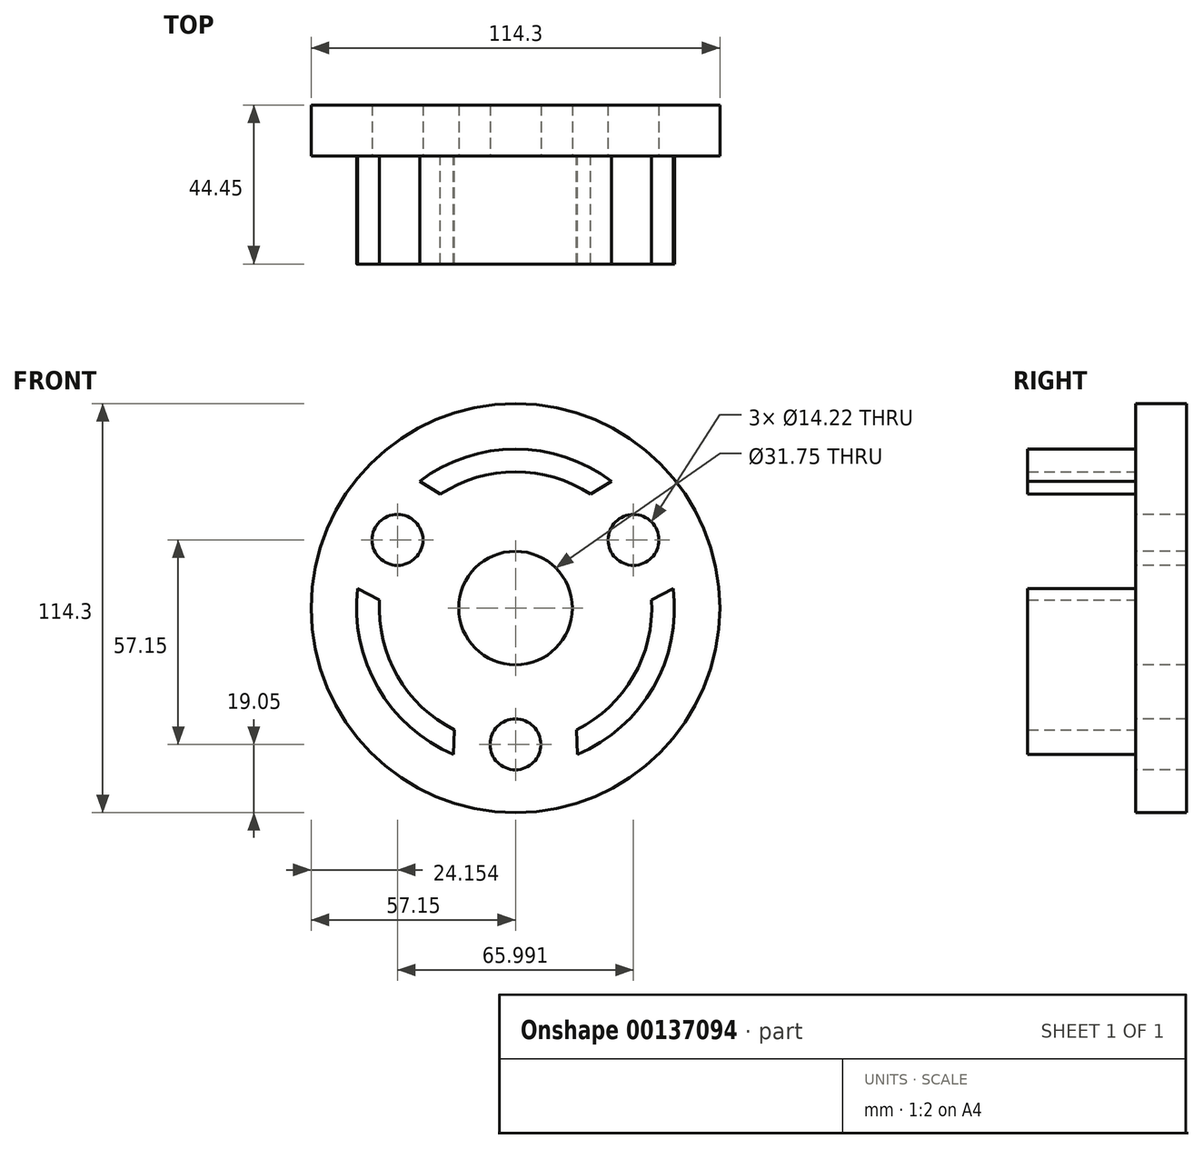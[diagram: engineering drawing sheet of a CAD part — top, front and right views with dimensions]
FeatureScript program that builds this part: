
annotation { "Feature Type Name" : "Feature", "Feature Type Description" : "" }
export const myFeature = defineFeature(function(context is Context, id is Id, definition is map)
    precondition{}
    {
        {
            var Q0;
            Q0=qCreatedBy(makeId("Front.planeOp"),FACE);
            var sketch = newSketch(context, id + "F0", { "sketchPlane" : qUnion([Q0])});
            skCircle(sketch, "E0", {"center": v(0, 0) * mm, "radius": 57.15 * mm});
            skSolve(sketch);
        }
        {
            var Q0;
            Q0 = qSketchRegion(id + "F0", true);
            extrude(context, id + "F1", {"entities" : qUnion([Q0]), "depth" : 14.22 * mm});
        }
        {
            var Q0;
            Q0=makeQuery(id+"F1.opExtrude","CAP_FACE",FACE,{"disambiguationData":[OSD([sQuery(id+"F0.wireOp",EDGE,"E0")])],"isStart":false});
            var sketch = newSketch(context, id + "F2", { "sketchPlane" : qUnion([Q0])});
            skCircle(sketch, "E1", {"center": v(0, 0) * mm, "radius": 15.88 * mm});
            skSolve(sketch);
        }
        {
            var Q0;
            Q0 = qSketchRegion(id + "F2", true);
            extrude(context, id + "F3", {"entities" : qUnion([Q0]), "operationType" : NewBodyOperationType.REMOVE, "oppositeDirection" : true, "depth" : 25.4 * mm});
        }
        {
            var Q0;
            Q0=makeQuery(id+"F1.opExtrude","CAP_FACE",FACE,{"disambiguationData":[OSD([sQuery(id+"F0.wireOp",EDGE,"E0")])],"isStart":false});
            var sketch = newSketch(context, id + "F4", { "sketchPlane" : qUnion([Q0])});
            skCircle(sketch, "E2", {"center": v(0, -38.1) * mm, "radius": 7.11 * mm});
            skCircle(sketch, "E3.1.0", {"center": v(33, 19.05) * mm, "radius": 7.11 * mm});
            skCircle(sketch, "E3.2.0", {"center": v(-33, 19.05) * mm, "radius": 7.11 * mm});
            skPoint(sketch, "E3.center", {"position": v(0, 0) * mm});
            skSolve(sketch);
        }
        {
            var Q0;
            Q0 = qSketchRegion(id + "F4", true);
            extrude(context, id + "F5", {"entities" : qUnion([Q0]), "operationType" : NewBodyOperationType.REMOVE, "oppositeDirection" : true, "depth" : 25.4 * mm});
        }
        {
            var Q0;
            Q0=makeQuery(id+"F2.imprint","IMPRINT",FACE,{"disambiguationData":[TD([[makeQuery(id+"F2.imprint","IMPRINT",EDGE,{"derivedFrom":sQuery(id+"F2.wireOp",EDGE,"E1")}),-1.0]])]});
            var sketch = newSketch(context, id + "F6", { "sketchPlane" : qUnion([Q0])});
            skArc(sketch, "E4", {"start": v(-44.1, 5.5) * mm, "mid": v(-38.5, -22.23) * mm, "end": v(-17.3, -40.95) * mm});
            skArc(sketch, "E5.trimOffspring", {"start": v(-38.03, 2.26) * mm, "mid": v(-33, -19.05) * mm, "end": v(-17.06, -34.07) * mm});
            skArc(sketch, "E6.trimOffspring", {"start": v(20.98, 31.8) * mm, "mid": v(0, 38.1) * mm, "end": v(-20.98, 31.8) * mm});
            skArc(sketch, "E7.trimOffspring", {"start": v(26.82, 35.45) * mm, "mid": v(0, 44.45) * mm, "end": v(-26.82, 35.45) * mm});
            skArc(sketch, "E8.trimOffspring", {"start": v(17.3, -40.95) * mm, "mid": v(38.5, -22.23) * mm, "end": v(44.1, 5.5) * mm});
            skArc(sketch, "E9.trimOffspring", {"start": v(17.06, -34.07) * mm, "mid": v(33, -19.05) * mm, "end": v(38.03, 2.26) * mm});
            skLineSegment(sketch, "E10", {"start": v(-44.1, 5.5) * mm, "end": v(-38.03, 2.26) * mm});
            skLineSegment(sketch, "E11", {"start": v(-17.3, -40.95) * mm, "end": v(-17.06, -34.07) * mm});
            skLineSegment(sketch, "E12", {"start": v(17.06, -34.07) * mm, "end": v(17.3, -40.95) * mm});
            skLineSegment(sketch, "E13", {"start": v(38.03, 2.26) * mm, "end": v(44.1, 5.5) * mm});
            skLineSegment(sketch, "E14", {"start": v(-26.82, 35.45) * mm, "end": v(-20.98, 31.8) * mm});
            skLineSegment(sketch, "E15", {"start": v(26.82, 35.45) * mm, "end": v(20.98, 31.8) * mm});
            skSolve(sketch);
        }
        {
            var Q0;
            Q0 = qSketchRegion(id + "F6", true);
            extrude(context, id + "F7", {"entities" : qUnion([Q0]), "operationType" : NewBodyOperationType.ADD, "depth" : 30.23 * mm});
        }
    });
